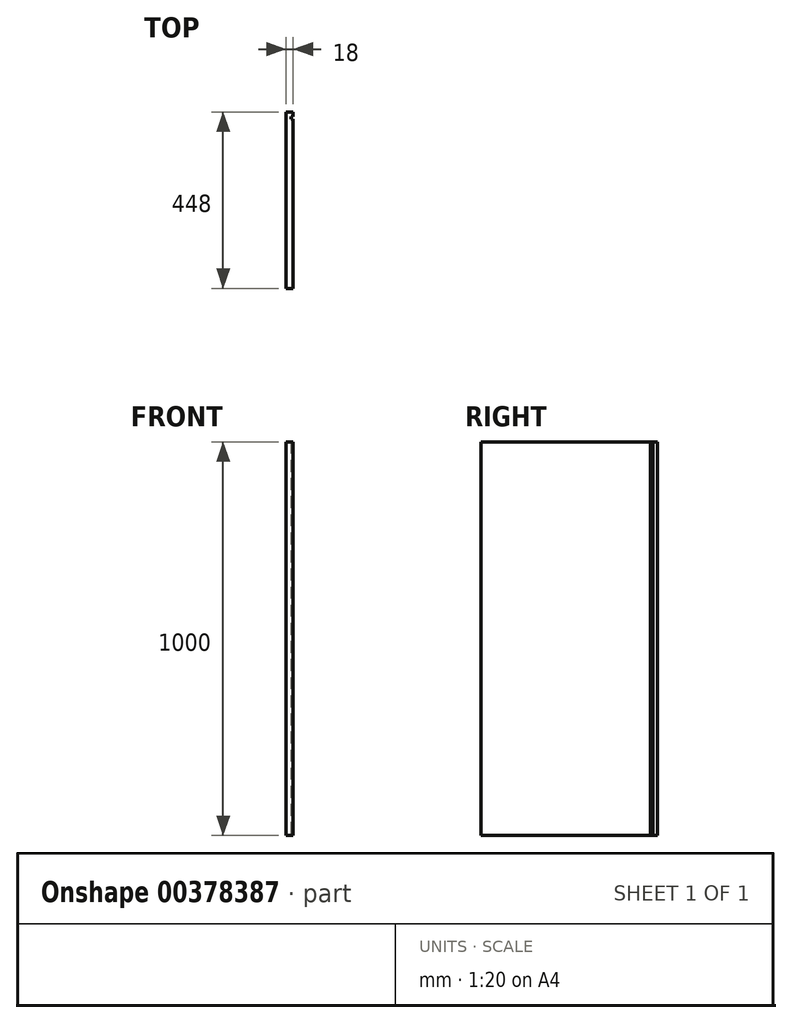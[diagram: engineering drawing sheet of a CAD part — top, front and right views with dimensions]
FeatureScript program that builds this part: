
annotation { "Feature Type Name" : "Feature", "Feature Type Description" : "" }
export const myFeature = defineFeature(function(context is Context, id is Id, definition is map)
    precondition{}
    {
        {
            var Q0;
            Q0=qCreatedBy(makeId("Top.planeOp"),FACE);
            var sketch = newSketch(context, id + "F0", { "sketchPlane" : qUnion([Q0])});
            skLineSegment(sketch, "E0.left", {"start": v(-9, 224) * mm, "end": v(-9, -224) * mm});
            skPoint(sketch, "E0.middle", {"position": v(0, 0) * mm});
            skLineSegment(sketch, "E1", {"start": v(-9, 224) * mm, "end": v(9, 224) * mm});
            skLineSegment(sketch, "E2", {"start": v(9, -224) * mm, "end": v(-9, -224) * mm});
            skLineSegment(sketch, "E3", {"start": v(9, 224) * mm, "end": v(9, 212) * mm});
            skLineSegment(sketch, "E4", {"start": v(9, 212) * mm, "end": v(3, 212) * mm});
            skLineSegment(sketch, "E5", {"start": v(3, 212) * mm, "end": v(3, 206) * mm});
            skLineSegment(sketch, "E6", {"start": v(3, 206) * mm, "end": v(9, 206) * mm});
            skLineSegment(sketch, "E7.trimOffspring", {"start": v(9, 206) * mm, "end": v(9, -224) * mm});
            skSolve(sketch);
        }
        {
            var Q0;
            Q0 = qSketchRegion(id + "F0", true);
            extrude(context, id + "F1", {"entities" : qUnion([Q0]), "depth" : 1000 * mm});
        }
    });
